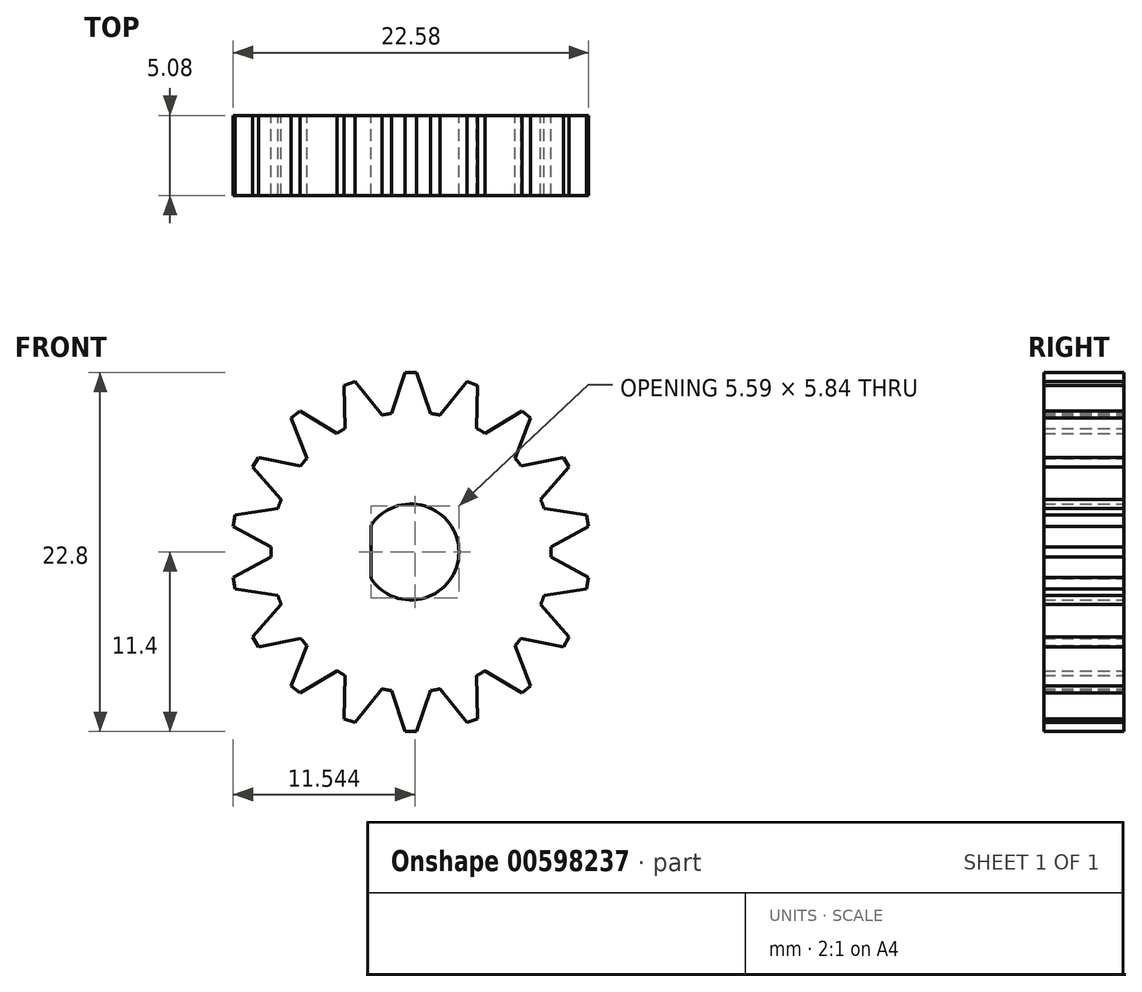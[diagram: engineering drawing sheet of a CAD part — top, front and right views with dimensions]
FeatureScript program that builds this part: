
annotation { "Feature Type Name" : "Feature", "Feature Type Description" : "" }
export const myFeature = defineFeature(function(context is Context, id is Id, definition is map)
    precondition{}
    {
        {
            var Q0;
            Q0=qCreatedBy(makeId("Front.planeOp"),FACE);
            var sketch = newSketch(context, id + "F0", { "sketchPlane" : qUnion([Q0])});
            skArc(sketch, "E0", {"start": v(-2.54, -1.68) * mm, "mid": v(3.05, 0) * mm, "end": v(-2.54, 1.68) * mm});
            skPoint(sketch, "E1", {"position": v(0, 3.05) * mm});
            skPoint(sketch, "E2", {"position": v(3.05, 0) * mm});
            skPoint(sketch, "E3", {"position": v(-3.05, 0) * mm});
            skLineSegment(sketch, "E4", {"start": v(-2.54, 1.68) * mm, "end": v(-2.54, -1.68) * mm});
            skCircle(sketch, "E5", {"center": v(0, 0) * mm, "radius": 8.9 * mm});
            skLineSegment(sketch, "E6.bottom", {"start": v(-0.36, 11.4) * mm, "end": v(0.36, 11.4) * mm});
            skPoint(sketch, "E6.middle", {"position": v(0, 8.36) * mm});
            skLineSegment(sketch, "E7", {"start": v(-0.36, 11.4) * mm, "end": v(-1.24, 8.8) * mm});
            skLineSegment(sketch, "E8.MirrorCS", {"start": v(0.36, 11.4) * mm, "end": v(1.24, 8.8) * mm});
            skPoint(sketch, "E6.top.start.orphan", {"position": v(-0.36, 5.32) * mm});
            skPoint(sketch, "E9.orphan", {"position": v(0.36, 5.32) * mm});
            skLineSegment(sketch, "E10.1.0", {"start": v(-4.24, 10.59) * mm, "end": v(-4.18, 7.85) * mm});
            skLineSegment(sketch, "E10.1.1", {"start": v(-4.24, 10.59) * mm, "end": v(-3.56, 10.84) * mm});
            skLineSegment(sketch, "E10.1.2", {"start": v(-3.56, 10.84) * mm, "end": v(-1.84, 8.7) * mm});
            skLineSegment(sketch, "E10.2.0", {"start": v(-7.6, 8.5) * mm, "end": v(-6.6, 5.95) * mm});
            skLineSegment(sketch, "E10.2.1", {"start": v(-7.6, 8.5) * mm, "end": v(-7.05, 8.97) * mm});
            skLineSegment(sketch, "E10.2.2", {"start": v(-7.05, 8.97) * mm, "end": v(-4.7, 7.54) * mm});
            skLineSegment(sketch, "E11.2.3.0", {"start": v(-10.05, 5.39) * mm, "end": v(-8.24, 3.33) * mm});
            skLineSegment(sketch, "E11.3.3.0", {"start": v(-10.05, 5.39) * mm, "end": v(-9.7, 6.01) * mm});
            skLineSegment(sketch, "E11.6.3.0", {"start": v(-9.7, 6.01) * mm, "end": v(-7, 5.48) * mm});
            skLineSegment(sketch, "E11.2.4.0", {"start": v(-11.29, 1.62) * mm, "end": v(-8.88, 0.3) * mm});
            skLineSegment(sketch, "E11.3.4.0", {"start": v(-11.29, 1.62) * mm, "end": v(-11.16, 2.34) * mm});
            skLineSegment(sketch, "E11.6.4.0", {"start": v(-11.16, 2.34) * mm, "end": v(-8.45, 2.75) * mm});
            skLineSegment(sketch, "E11.2.5.0", {"start": v(-11.16, -2.34) * mm, "end": v(-8.45, -2.75) * mm});
            skLineSegment(sketch, "E11.3.5.0", {"start": v(-11.16, -2.34) * mm, "end": v(-11.29, -1.62) * mm});
            skLineSegment(sketch, "E11.6.5.0", {"start": v(-11.29, -1.62) * mm, "end": v(-8.88, -0.3) * mm});
            skLineSegment(sketch, "E11.2.6.0", {"start": v(-9.7, -6.01) * mm, "end": v(-7, -5.48) * mm});
            skLineSegment(sketch, "E11.3.6.0", {"start": v(-9.7, -6.01) * mm, "end": v(-10.05, -5.39) * mm});
            skLineSegment(sketch, "E11.6.6.0", {"start": v(-10.05, -5.39) * mm, "end": v(-8.24, -3.33) * mm});
            skLineSegment(sketch, "E11.2.7.0", {"start": v(-7.05, -8.97) * mm, "end": v(-4.7, -7.54) * mm});
            skLineSegment(sketch, "E11.3.7.0", {"start": v(-7.05, -8.97) * mm, "end": v(-7.6, -8.5) * mm});
            skLineSegment(sketch, "E11.6.7.0", {"start": v(-7.6, -8.5) * mm, "end": v(-6.6, -5.95) * mm});
            skLineSegment(sketch, "E11.2.8.0", {"start": v(-3.56, -10.84) * mm, "end": v(-1.84, -8.7) * mm});
            skLineSegment(sketch, "E11.3.8.0", {"start": v(-3.56, -10.84) * mm, "end": v(-4.24, -10.59) * mm});
            skLineSegment(sketch, "E11.6.8.0", {"start": v(-4.24, -10.59) * mm, "end": v(-4.18, -7.85) * mm});
            skLineSegment(sketch, "E11.2.9.0", {"start": v(0.36, -11.4) * mm, "end": v(1.24, -8.8) * mm});
            skLineSegment(sketch, "E11.3.9.0", {"start": v(0.36, -11.4) * mm, "end": v(-0.36, -11.4) * mm});
            skLineSegment(sketch, "E11.6.9.0", {"start": v(-0.36, -11.4) * mm, "end": v(-1.24, -8.8) * mm});
            skLineSegment(sketch, "E11.2.10.0", {"start": v(4.24, -10.59) * mm, "end": v(4.18, -7.85) * mm});
            skLineSegment(sketch, "E11.3.10.0", {"start": v(4.24, -10.59) * mm, "end": v(3.56, -10.84) * mm});
            skLineSegment(sketch, "E11.6.10.0", {"start": v(3.56, -10.84) * mm, "end": v(1.84, -8.7) * mm});
            skLineSegment(sketch, "E11.2.11.0", {"start": v(7.6, -8.5) * mm, "end": v(6.6, -5.95) * mm});
            skLineSegment(sketch, "E11.3.11.0", {"start": v(7.6, -8.5) * mm, "end": v(7.05, -8.97) * mm});
            skLineSegment(sketch, "E11.6.11.0", {"start": v(7.05, -8.97) * mm, "end": v(4.7, -7.54) * mm});
            skLineSegment(sketch, "E12.2.12.0", {"start": v(10.05, -5.39) * mm, "end": v(8.24, -3.33) * mm});
            skLineSegment(sketch, "E12.3.12.0", {"start": v(10.05, -5.39) * mm, "end": v(9.7, -6.01) * mm});
            skLineSegment(sketch, "E12.6.12.0", {"start": v(9.7, -6.01) * mm, "end": v(7, -5.48) * mm});
            skLineSegment(sketch, "E12.2.13.0", {"start": v(11.29, -1.62) * mm, "end": v(8.88, -0.3) * mm});
            skLineSegment(sketch, "E12.3.13.0", {"start": v(11.29, -1.62) * mm, "end": v(11.16, -2.34) * mm});
            skLineSegment(sketch, "E12.6.13.0", {"start": v(11.16, -2.34) * mm, "end": v(8.45, -2.75) * mm});
            skLineSegment(sketch, "E13.2.14.0", {"start": v(11.16, 2.34) * mm, "end": v(8.45, 2.75) * mm});
            skLineSegment(sketch, "E13.3.14.0", {"start": v(11.16, 2.34) * mm, "end": v(11.29, 1.62) * mm});
            skLineSegment(sketch, "E13.6.14.0", {"start": v(11.29, 1.62) * mm, "end": v(8.88, 0.3) * mm});
            skLineSegment(sketch, "E13.2.15.0", {"start": v(9.7, 6.01) * mm, "end": v(7, 5.48) * mm});
            skLineSegment(sketch, "E13.3.15.0", {"start": v(9.7, 6.01) * mm, "end": v(10.05, 5.39) * mm});
            skLineSegment(sketch, "E13.6.15.0", {"start": v(10.05, 5.39) * mm, "end": v(8.24, 3.33) * mm});
            skLineSegment(sketch, "E14.2.16.0", {"start": v(7.05, 8.97) * mm, "end": v(4.7, 7.54) * mm});
            skLineSegment(sketch, "E14.3.16.0", {"start": v(7.05, 8.97) * mm, "end": v(7.6, 8.5) * mm});
            skLineSegment(sketch, "E14.6.16.0", {"start": v(7.6, 8.5) * mm, "end": v(6.6, 5.95) * mm});
            skLineSegment(sketch, "E14.2.17.0", {"start": v(3.56, 10.84) * mm, "end": v(1.84, 8.7) * mm});
            skLineSegment(sketch, "E14.3.17.0", {"start": v(3.56, 10.84) * mm, "end": v(4.24, 10.59) * mm});
            skLineSegment(sketch, "E14.6.17.0", {"start": v(4.24, 10.59) * mm, "end": v(4.18, 7.85) * mm});
            skSolve(sketch);
        }
        {
            var Q0;
            Q0=makeQuery(id+"F0.imprint","IMPRINT",FACE,{"disambiguationData":[TD([[makeQuery(id+"F0.imprint","IMPRINT",EDGE,{"derivedFrom":sQuery(id+"F0.wireOp",EDGE,"E0")}),-1.0]])]});
            var Q1;
            {var subQ0=sQuery(id+"F0.wireOp",EDGE,"E14.2.17.0");Q1=makeQuery(id+"F0.imprint","IMPRINT",FACE,{"disambiguationData":[TD([[makeQuery(id+"F0.imprint","IMPRINT",EDGE,{"derivedFrom":subQ0}),1.0]])]});}
            var Q2;
            Q2=makeQuery(id+"F0.imprint","IMPRINT",FACE,{"disambiguationData":[TD([[makeQuery(id+"F0.imprint","IMPRINT",EDGE,{"derivedFrom":sQuery(id+"F0.wireOp",EDGE,"E6.bottom")}),-1.0]])]});
            var Q3;
            {var subQ0=sQuery(id+"F0.wireOp",EDGE,"E10.1.0");Q3=makeQuery(id+"F0.imprint","IMPRINT",FACE,{"disambiguationData":[TD([[makeQuery(id+"F0.imprint","IMPRINT",EDGE,{"derivedFrom":subQ0}),1.0]])]});}
            var Q4;
            {var subQ0=sQuery(id+"F0.wireOp",EDGE,"E10.2.0");Q4=makeQuery(id+"F0.imprint","IMPRINT",FACE,{"disambiguationData":[TD([[makeQuery(id+"F0.imprint","IMPRINT",EDGE,{"derivedFrom":subQ0}),1.0]])]});}
            var Q5;
            {var subQ0=sQuery(id+"F0.wireOp",EDGE,"E11.2.3.0");Q5=makeQuery(id+"F0.imprint","IMPRINT",FACE,{"disambiguationData":[TD([[makeQuery(id+"F0.imprint","IMPRINT",EDGE,{"derivedFrom":subQ0}),1.0]])]});}
            var Q6;
            {var subQ0=sQuery(id+"F0.wireOp",EDGE,"E11.2.4.0");Q6=makeQuery(id+"F0.imprint","IMPRINT",FACE,{"disambiguationData":[TD([[makeQuery(id+"F0.imprint","IMPRINT",EDGE,{"derivedFrom":subQ0}),1.0]])]});}
            var Q7;
            {var subQ0=sQuery(id+"F0.wireOp",EDGE,"E11.2.5.0");Q7=makeQuery(id+"F0.imprint","IMPRINT",FACE,{"disambiguationData":[TD([[makeQuery(id+"F0.imprint","IMPRINT",EDGE,{"derivedFrom":subQ0}),1.0]])]});}
            var Q8;
            {var subQ0=sQuery(id+"F0.wireOp",EDGE,"E11.2.6.0");Q8=makeQuery(id+"F0.imprint","IMPRINT",FACE,{"disambiguationData":[TD([[makeQuery(id+"F0.imprint","IMPRINT",EDGE,{"derivedFrom":subQ0}),1.0]])]});}
            var Q9;
            {var subQ0=sQuery(id+"F0.wireOp",EDGE,"E11.2.7.0");Q9=makeQuery(id+"F0.imprint","IMPRINT",FACE,{"disambiguationData":[TD([[makeQuery(id+"F0.imprint","IMPRINT",EDGE,{"derivedFrom":subQ0}),1.0]])]});}
            var Q10;
            {var subQ0=sQuery(id+"F0.wireOp",EDGE,"E11.2.8.0");Q10=makeQuery(id+"F0.imprint","IMPRINT",FACE,{"disambiguationData":[TD([[makeQuery(id+"F0.imprint","IMPRINT",EDGE,{"derivedFrom":subQ0}),1.0]])]});}
            var Q11;
            {var subQ0=sQuery(id+"F0.wireOp",EDGE,"E11.2.10.0");Q11=makeQuery(id+"F0.imprint","IMPRINT",FACE,{"disambiguationData":[TD([[makeQuery(id+"F0.imprint","IMPRINT",EDGE,{"derivedFrom":subQ0}),1.0]])]});}
            var Q12;
            {var subQ0=sQuery(id+"F0.wireOp",EDGE,"E11.2.11.0");Q12=makeQuery(id+"F0.imprint","IMPRINT",FACE,{"disambiguationData":[TD([[makeQuery(id+"F0.imprint","IMPRINT",EDGE,{"derivedFrom":subQ0}),1.0]])]});}
            var Q13;
            {var subQ0=sQuery(id+"F0.wireOp",EDGE,"E12.2.12.0");Q13=makeQuery(id+"F0.imprint","IMPRINT",FACE,{"disambiguationData":[TD([[makeQuery(id+"F0.imprint","IMPRINT",EDGE,{"derivedFrom":subQ0}),1.0]])]});}
            var Q14;
            {var subQ0=sQuery(id+"F0.wireOp",EDGE,"E12.2.13.0");Q14=makeQuery(id+"F0.imprint","IMPRINT",FACE,{"disambiguationData":[TD([[makeQuery(id+"F0.imprint","IMPRINT",EDGE,{"derivedFrom":subQ0}),1.0]])]});}
            var Q15;
            {var subQ0=sQuery(id+"F0.wireOp",EDGE,"E13.2.15.0");Q15=makeQuery(id+"F0.imprint","IMPRINT",FACE,{"disambiguationData":[TD([[makeQuery(id+"F0.imprint","IMPRINT",EDGE,{"derivedFrom":subQ0}),1.0]])]});}
            var Q16;
            {var subQ0=sQuery(id+"F0.wireOp",EDGE,"E14.2.16.0");Q16=makeQuery(id+"F0.imprint","IMPRINT",FACE,{"disambiguationData":[TD([[makeQuery(id+"F0.imprint","IMPRINT",EDGE,{"derivedFrom":subQ0}),1.0]])]});}
            var Q17;
            {var subQ0=sQuery(id+"F0.wireOp",EDGE,"E13.2.14.0");Q17=makeQuery(id+"F0.imprint","IMPRINT",FACE,{"disambiguationData":[TD([[makeQuery(id+"F0.imprint","IMPRINT",EDGE,{"derivedFrom":subQ0}),1.0]])]});}
            var Q18;
            {var subQ0=sQuery(id+"F0.wireOp",EDGE,"E11.2.9.0");Q18=makeQuery(id+"F0.imprint","IMPRINT",FACE,{"disambiguationData":[TD([[makeQuery(id+"F0.imprint","IMPRINT",EDGE,{"derivedFrom":subQ0}),1.0]])]});}
            extrude(context, id + "F1", {"entities" : qUnion([Q0, Q1, Q2, Q3, Q4, Q5, Q6, Q7, Q8, Q9, Q10, Q11, Q12, Q13, Q14, Q15, Q16, Q17, Q18]), "endBound" : BoundingType.SYMMETRIC, "depth" : 5.08 * mm, "offsetDistance" : 25.4 * mm});
        }
    });
